# Revit family: 751290001_Válvula para Orinal Push Entrada Superior Empotrada
name_source: partatom
category: Plumbing Fixtures
units: mm (PartAtom-declared; Revit-internal decimal feet)

## family parameters
Always vertical = Yes
Cut with Voids When Loaded = No
Host = Wall
OmniClass Number = 23.45.05.14.99
OmniClass Title = Other Sanitary Washing Plumbing Fixtures
Part Type = Normal
Room Calculation Point = No
Round Connector Dimension = Use Diameter
Shared = No

## types (1)
- Type 1
    Alto = 384 mm
    Ancho = 74 mm
    Capacidad de flujo = 6,35 - 9,68 L/min - 0,33 - 0,49 L/Descarga.
    Creado por = IDD
    Fabricante = Corona
    Fecha de creación = 31/07/2020
    Garantía = 3 años
    Material = Corona_Acero
    Peso Bruto aprox = 1030g 2,27lb
    Peso Neto aprox = 895g 1,97lb
    Presion maxima = 80 Psi
    Presion minima = 20 Psi
    Profundidad = 117 mm
    URL = https://corona.co

## geometry (parser evidence)
native form markers: Sweep x4
no freeform markers — native parametric forms only
